# Revit family: LFX_A3-M-Suspended-Linear-2
name_source: partatom
category: Lighting Fixtures
revit_build: Autodesk Revit 2016 (Build: 20150220_1215(x64)
units: mm (PartAtom-declared; Revit-internal decimal feet)

## family parameters
Always vertical = Yes
Cut with Voids When Loaded = No
Host = Ceiling
Light Source = Yes
Part Type = Normal
Room Calculation Point = No
Round Connector Dimension = Use Diameter
Shared = No

## types (3) — shared parameters
Ceiling Mount = Metal - Paint Finish - Ivory, Glossy
Color Filter = 16777215
Diffuser = Glass - White, High Luminance
Dimming Lamp Color Temperature Shift = <None>
Emit from Line Length = 1048 mm
Light Casing = Metal - Paint Finish - Ivory, Glossy
Light Fixture Height = 1800 mm  [stored 5.90551 ft]
Light Source Symbol Size = 610 mm

## per-type parameters (varying)
| type | Length |
| 1200mm | 1200 mm |
| 2400mm | 2400 mm  [stored 7.87402 ft] |
| Ceiling Linear | 1200 mm |

note: [stored X ft] marks values corroborated as IEEE doubles in the binary element streams (Revit-internal decimal feet)

## geometry (parser evidence)
native form markers: Sweep x1
no freeform markers — native parametric forms only
